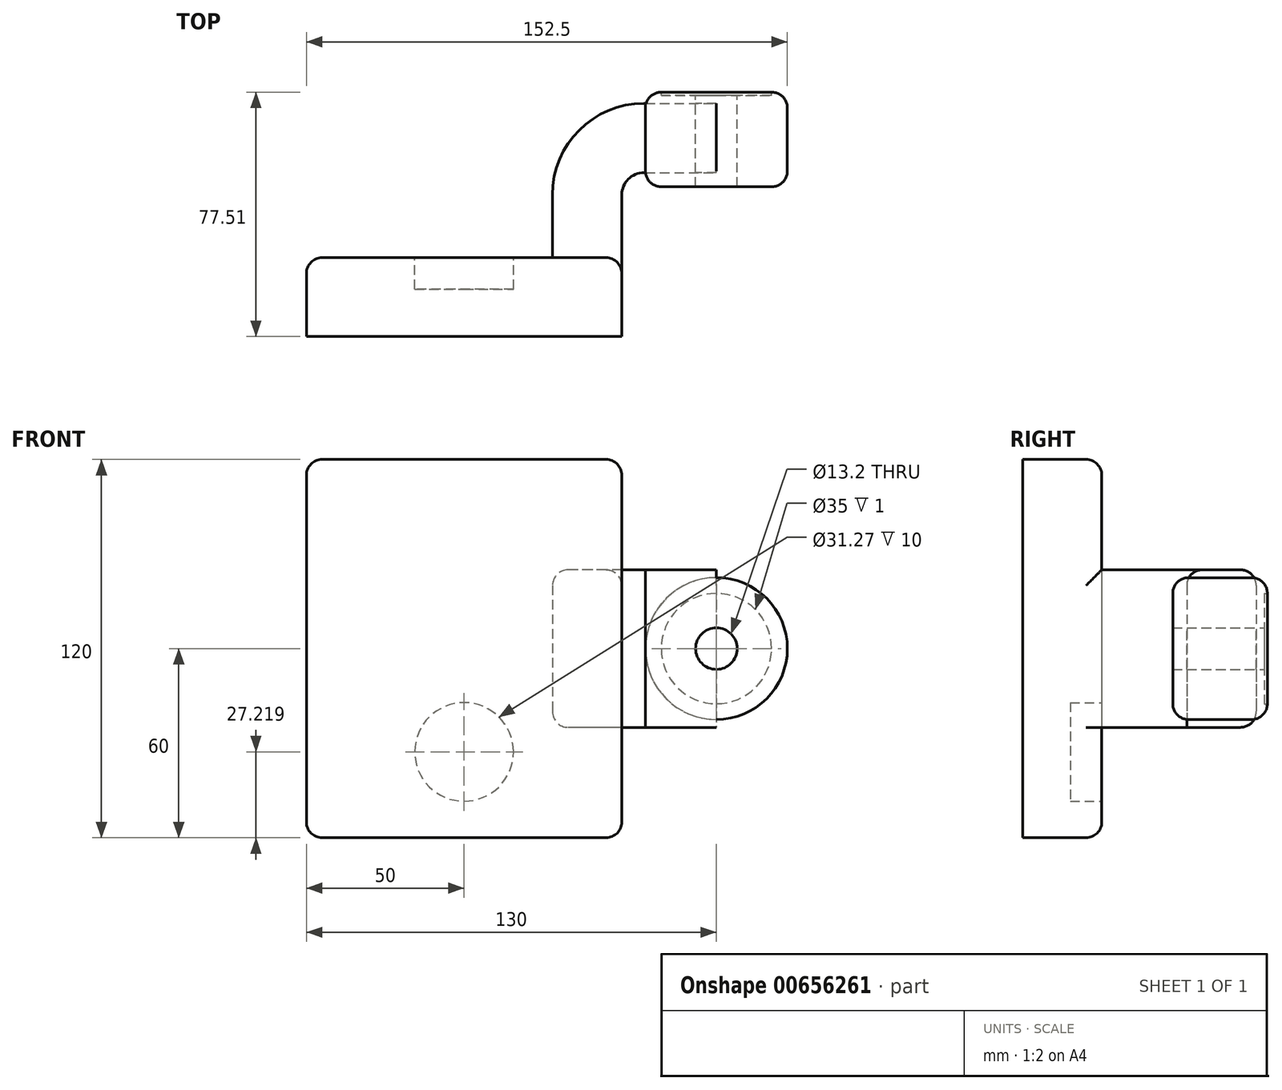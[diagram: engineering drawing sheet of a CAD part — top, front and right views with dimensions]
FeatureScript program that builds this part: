
annotation { "Feature Type Name" : "Feature", "Feature Type Description" : "" }
export const myFeature = defineFeature(function(context is Context, id is Id, definition is map)
    precondition{}
    {
        {
            var Q0;
            Q0=qCreatedBy(makeId("Top.planeOp"),FACE);
            var sketch = newSketch(context, id + "F0", { "sketchPlane" : qUnion([Q0])});
            skLineSegment(sketch, "E0.bottom", {"start": v(50, -12.5) * mm, "end": v(-50, -12.5) * mm});
            skLineSegment(sketch, "E0.top", {"start": v(50, 12.5) * mm, "end": v(-50, 12.5) * mm});
            skLineSegment(sketch, "E0.left", {"start": v(50, -12.5) * mm, "end": v(50, 12.5) * mm});
            skLineSegment(sketch, "E0.right", {"start": v(-50, -12.5) * mm, "end": v(-50, 12.5) * mm});
            skPoint(sketch, "E0.middle", {"position": v(0, 0) * mm});
            skLineSegment(sketch, "E1.bottom", {"start": v(102.5, 35.01) * mm, "end": v(57.5, 35.01) * mm});
            skLineSegment(sketch, "E1.top", {"start": v(102.5, 65.01) * mm, "end": v(57.5, 65.01) * mm});
            skLineSegment(sketch, "E1.left", {"start": v(102.5, 35.01) * mm, "end": v(102.5, 65.01) * mm});
            skLineSegment(sketch, "E1.right", {"start": v(57.5, 35.01) * mm, "end": v(57.5, 65.01) * mm});
            skPoint(sketch, "E1.middle", {"position": v(80, 50.01) * mm});
            skLineSegment(sketch, "E2", {"start": v(50, 12.5) * mm, "end": v(50, 32.46) * mm});
            skArc(sketch, "E3", {"start": v(50, 32.46) * mm, "mid": v(52.05, 37.41) * mm, "end": v(57, 39.46) * mm});
            skLineSegment(sketch, "E4", {"start": v(57, 39.46) * mm, "end": v(80, 39.46) * mm});
            skLineSegment(sketch, "E5.0", {"start": v(57, 61.46) * mm, "end": v(80, 61.46) * mm});
            skArc(sketch, "E5.1", {"start": v(28, 32.46) * mm, "mid": v(36.5, 52.97) * mm, "end": v(57, 61.46) * mm});
            skLineSegment(sketch, "E5.2", {"start": v(28, 12.5) * mm, "end": v(28, 32.46) * mm});
            skFitSpline(sketch, "E6", {"points": [v(-50, 12.5) * mm, v(57, 61.46) * mm], "startDerivative": vector(71.48, 99.9) * mm, "endDerivative": vector(111.8, -6.45) * mm});
            skLineSegment(sketch, "E7", {"start": v(80, 35.01) * mm, "end": v(80, 65.01) * mm});
            skSolve(sketch);
        }
        {
            var Q0;
            Q0=makeQuery(id+"F0.imprint","IMPRINT",FACE,{"disambiguationData":[TD([[makeQuery(id+"F0.imprint","IMPRINT",EDGE,{"derivedFrom":sQuery(id+"F0.wireOp",EDGE,"E5.1")}),1.0]])]});
            extrude(context, id + "F1", {"entities" : qUnion([Q0]), "endBound" : BoundingType.SYMMETRIC, "depth" : 25 * mm, "offsetDistance" : 25 * mm});
        }
        {
            var Q0;
            Q0=makeQuery(id+"F0.imprint","IMPRINT",FACE,{"disambiguationData":[TD([[makeQuery(id+"F0.imprint","IMPRINT",EDGE,{"derivedFrom":sQuery(id+"F0.wireOp",EDGE,"E0.bottom")}),-1.0]])]});
            extrude(context, id + "F2", {"entities" : qUnion([Q0]), "operationType" : NewBodyOperationType.ADD, "endBound" : BoundingType.SYMMETRIC, "depth" : 120 * mm, "offsetDistance" : 25 * mm});
        }
        {
            var Q0;
            {var subQ1=sQuery(id+"F0.wireOp",EDGE,"E2");Q0=makeQuery(id+"F0.imprint","IMPRINT",FACE,{"disambiguationData":[TD([[makeQuery(id+"F0.imprint","IMPRINT",EDGE,{"derivedFrom":subQ1}),1.0]])]});}
            extrude(context, id + "F3", {"entities" : qUnion([Q0]), "operationType" : NewBodyOperationType.ADD, "endBound" : BoundingType.SYMMETRIC, "depth" : 50 * mm, "offsetDistance" : 25 * mm});
        }
        {
            var Q0;
            {var subQ0=sQuery(id+"F0.wireOp",EDGE,"E1.left");Q0=makeQuery(id+"F0.imprint","IMPRINT",FACE,{"disambiguationData":[TD([[makeQuery(id+"F0.imprint","IMPRINT",EDGE,{"derivedFrom":subQ0}),1.0]])]});}
            var Q1;
            Q1=sQuery(id+"F0.wireOp",EDGE,"E7");
            revolve(context, id + "F4", {"operationType" : NewBodyOperationType.ADD, "entities" : qUnion([Q0]), "axis" : qUnion([Q1]), "revolveType" : RevolveType.FULL});
        }
        {
            var Q0;
            {var subQ0=sQuery(id+"F0.wireOp",EDGE,"E4");var subQ1=sQuery(id+"F0.wireOp",EDGE,"E1.right");var subQ2=makeQuery(id+"F0.imprint","INTERSECT",VERTEX,{"derivedFrom":[subQ1,subQ0]});Q0=makeQuery(id+"F0.imprint","IMPRINT",FACE,{"disambiguationData":[TD([[makeQuery(id+"F0.imprint","IMPRINT",EDGE,{"disambiguationData":[TD([[subQ2,-1.0]])],"derivedFrom":subQ1}),-1.0]])]});}
            extrude(context, id + "F5", {"entities" : qUnion([Q0]), "endBound" : BoundingType.SYMMETRIC, "depth" : 50 * mm, "offsetDistance" : 25 * mm});
        }
        {
            var Q0;
            Q0=makeQuery(id+"F2.opExtrude","CAP_EDGE",EDGE,{"disambiguationData":[OSD([sQuery(id+"F0.wireOp",EDGE,"E0.right")])],"isStart":false});
            var Q1;
            Q1=makeQuery(id+"F2.opExtrude","CAP_EDGE",EDGE,{"disambiguationData":[OSD([sQuery(id+"F0.wireOp",EDGE,"E0.left")])],"isStart":false});
            var Q2;
            Q2=makeQuery(id+"F2.opExtrude","CAP_EDGE",EDGE,{"disambiguationData":[OSD([sQuery(id+"F0.wireOp",EDGE,"E0.left")])],"isStart":true});
            var Q3;
            Q3=makeQuery(id+"F2.opExtrude","CAP_EDGE",EDGE,{"disambiguationData":[OSD([sQuery(id+"F0.wireOp",EDGE,"E0.right")])],"isStart":true});
            var Q4;
            Q4=makeQuery(id+"F4.opRevolve","SWEPT_FACE",FACE,{"disambiguationData":[OSD([sQuery(id+"F0.wireOp",EDGE,"E1.top")])]});
            var Q5;
            Q5=makeQuery(id+"F4.opRevolve","SWEPT_FACE",FACE,{"disambiguationData":[OSD([sQuery(id+"F0.wireOp",EDGE,"E1.bottom")])]});
            var Q6;
            Q6=makeQuery(id+"F1.opExtrude","CAP_EDGE",EDGE,{"disambiguationData":[OSD([sQuery(id+"F0.wireOp",EDGE,"E6")])],"isStart":false});
            var Q7;
            Q7=makeQuery(id+"F1.opExtrude","CAP_EDGE",EDGE,{"disambiguationData":[OSD([sQuery(id+"F0.wireOp",EDGE,"E6")])],"isStart":true});
            var Q8;
            Q8=makeQuery(id+"F3.opExtrude","CAP_EDGE",EDGE,{"disambiguationData":[OSD([sQuery(id+"F0.wireOp",EDGE,"E5.1")])],"isStart":false});
            var Q9;
            Q9=makeQuery(id+"F5.opExtrude","CAP_EDGE",EDGE,{"disambiguationData":[OSD([sQuery(id+"F0.wireOp",EDGE,"E5.0")])],"isStart":false});
            var Q10;
            Q10=makeQuery(id+"F5.opExtrude","CAP_EDGE",EDGE,{"disambiguationData":[OSD([sQuery(id+"F0.wireOp",EDGE,"E4")])],"isStart":false});
            var Q11;
            Q11=makeQuery(id+"F3.opExtrude","CAP_EDGE",EDGE,{"disambiguationData":[OSD([sQuery(id+"F0.wireOp",EDGE,"E3")])],"isStart":false});
            var Q12;
            {var subQ0=sQuery(id+"F0.wireOp",EDGE,"E2");var subQ1=sQuery(id+"F0.wireOp",EDGE,"E0.top");var subQ2=sQuery(id+"F0.wireOp",EDGE,"E0.left");Q12=makeQuery(id+"F3.boolean.opBoolean","SPLIT",EDGE,{"disambiguationData":[TD([makeQuery(id+"F2.opExtrude","CAP_FACE",FACE,{"disambiguationData":[OSD([sQuery(id+"F0.wireOp",EDGE,"E0.bottom"),subQ1,subQ2,sQuery(id+"F0.wireOp",EDGE,"E0.right")])],"isStart":false})])],"derivedFrom":makeQuery(id+"F2.opExtrude","SWEPT_EDGE",EDGE,{"disambiguationData":[OSD([subQ1,subQ2,subQ0])]})});}
            var Q13;
            Q13=makeQuery(id+"F2.opExtrude","CAP_EDGE",EDGE,{"disambiguationData":[OSD([sQuery(id+"F0.wireOp",EDGE,"E0.top")])],"isStart":false});
            var Q14;
            {var subQ0=sQuery(id+"F0.wireOp",EDGE,"E0.left");var subQ1=sQuery(id+"F0.wireOp",EDGE,"E2");var subQ2=sQuery(id+"F0.wireOp",EDGE,"E0.top");Q14=makeQuery(id+"F3.boolean.opBoolean","SPLIT",EDGE,{"disambiguationData":[TD([makeQuery(id+"F2.opExtrude","CAP_FACE",FACE,{"disambiguationData":[OSD([sQuery(id+"F0.wireOp",EDGE,"E0.bottom"),subQ2,subQ0,sQuery(id+"F0.wireOp",EDGE,"E0.right")])],"isStart":true})])],"derivedFrom":makeQuery(id+"F2.opExtrude","SWEPT_EDGE",EDGE,{"disambiguationData":[OSD([subQ2,subQ0,subQ1])]})});}
            var Q15;
            Q15=makeQuery(id+"F2.opExtrude","CAP_EDGE",EDGE,{"disambiguationData":[OSD([sQuery(id+"F0.wireOp",EDGE,"E0.top")])],"isStart":true});
            fillet(context, id + "F6", {"entities" : qUnion([Q0, Q1, Q2, Q3, Q4, Q5, Q6, Q7, Q8, Q9, Q10, Q11, Q12, Q13, Q14, Q15]), "radius" : 5 * mm, "tangentPropagation" : true, "allowEdgeOverflow" : false});
        }
        {
            var Q0;
            {var subQ0=sQuery(id+"F0.wireOp",EDGE,"E0.top");var subQ1=sQuery(id+"F0.wireOp",EDGE,"E0.right");var subQ2=sQuery(id+"F0.wireOp",EDGE,"E6");Q0=makeQuery(id+"F2.boolean.opBoolean","SPLIT",EDGE,{"disambiguationData":[TD([makeQuery(id+"F1.opExtrude","CAP_FACE",FACE,{"disambiguationData":[OSD([subQ0,sQuery(id+"F0.wireOp",EDGE,"E5.1"),sQuery(id+"F0.wireOp",EDGE,"E5.2"),subQ2])],"isStart":false})])],"derivedFrom":makeQuery(id+"F2.opExtrude","SWEPT_EDGE",EDGE,{"disambiguationData":[OSD([subQ0,subQ1,subQ2])]})});}
            var Q1;
            {var subQ0=sQuery(id+"F0.wireOp",EDGE,"E0.top");var subQ1=sQuery(id+"F0.wireOp",EDGE,"E0.right");var subQ2=sQuery(id+"F0.wireOp",EDGE,"E6");Q1=makeQuery(id+"F2.boolean.opBoolean","SPLIT",EDGE,{"disambiguationData":[TD([makeQuery(id+"F1.opExtrude","CAP_FACE",FACE,{"disambiguationData":[OSD([subQ0,sQuery(id+"F0.wireOp",EDGE,"E5.1"),sQuery(id+"F0.wireOp",EDGE,"E5.2"),subQ2])],"isStart":true})])],"derivedFrom":makeQuery(id+"F2.opExtrude","SWEPT_EDGE",EDGE,{"disambiguationData":[OSD([subQ0,subQ1,subQ2])]})});}
            fillet(context, id + "F7", {"entities" : qUnion([Q0, Q1]), "radius" : 5 * mm, "tangentPropagation" : true, "allowEdgeOverflow" : false});
        }
        {
            var Q0;
            Q0=makeQuery(id+"F4.opRevolve","SWEPT_FACE",FACE,{"disambiguationData":[OSD([sQuery(id+"F0.wireOp",EDGE,"E1.top")])]});
            var sketch = newSketch(context, id + "F8", { "sketchPlane" : qUnion([Q0])});
            skPoint(sketch, "E8", {"position": v(-80, 0) * mm});
            skSolve(sketch);
        }
        {
            var Q0;
            Q0=sQuery(id+"F8.wireOp",VERTEX,"E8");
            var Q1;
            Q1=makeQuery(id+"F4.opRevolve","SWEPT_BODY",BODY,{"disambiguationData":[OSD([sQuery(id+"F0.wireOp",EDGE,"E1.bottom"),sQuery(id+"F0.wireOp",EDGE,"E1.top"),sQuery(id+"F0.wireOp",EDGE,"E1.left"),sQuery(id+"F0.wireOp",EDGE,"E7")])]});
            var Q2;
            Q2=makeQuery(id+"F5.opExtrude","SWEPT_BODY",BODY,{"disambiguationData":[OSD([sQuery(id+"F0.wireOp",EDGE,"E1.right"),sQuery(id+"F0.wireOp",EDGE,"E4"),sQuery(id+"F0.wireOp",EDGE,"E5.0"),sQuery(id+"F0.wireOp",EDGE,"E7")])]});
            hole(context, id + "F9", {"style" : HoleStyle.SIMPLE, "endStyle" : HoleEndStyle.THROUGH, "standardTappedOrClearance" : lookupTablePath({ "standard" : "ISO", "fit" : "Normal", "size" : "M12", "type" : "Clearance" }), "standardBlindInLast" : lookupTablePath({ "fit" : "Standard", "standard" : "ISO", "size" : "M12", "type" : "Clearance" }), "holeDiameter" : 13.2 * mm, "majorDiameter" : 10 * mm, "isTappedThrough" : true, "tappedDepth" : 12 * mm, "tapClearance" : 3, "startFromSketch" : true, "locations" : qUnion([Q0]), "scope" : qUnion([Q1, Q2])});
        }
        {
            var Q0;
            Q0=makeQuery(id+"F5.opExtrude","CAP_EDGE",EDGE,{"disambiguationData":[OSD([sQuery(id+"F0.wireOp",EDGE,"E5.0")])],"isStart":true});
            var Q1;
            Q1=makeQuery(id+"F3.opExtrude","CAP_EDGE",EDGE,{"disambiguationData":[OSD([sQuery(id+"F0.wireOp",EDGE,"E5.1")])],"isStart":true});
            fillet(context, id + "F10", {"entities" : qUnion([Q0, Q1]), "radius" : 5 * mm, "tangentPropagation" : true, "allowEdgeOverflow" : false});
        }
        {
            var Q0;
            Q0=makeQuery(id+"F4.opRevolve","SWEPT_FACE",FACE,{"disambiguationData":[OSD([sQuery(id+"F0.wireOp",EDGE,"E1.top")])]});
            extrude(context, id + "F11", {"entities" : qUnion([Q0]), "operationType" : NewBodyOperationType.REMOVE, "oppositeDirection" : true, "depth" : 1 * mm, "offsetDistance" : 25 * mm});
        }
        {
            var Q0;
            {var subQ2=sQuery(id+"F0.wireOp",EDGE,"E0.top");var subQ3=sQuery(id+"F0.wireOp",EDGE,"E6");var subQ5=sQuery(id+"F0.wireOp",EDGE,"E5.2");var subQ6=sQuery(id+"F0.wireOp",EDGE,"E5.1");Q0=makeQuery(id+"F3.boolean.opBoolean","SPLIT",FACE,{"disambiguationData":[TD([makeQuery(id+"F1.opExtrude","CAP_FACE",FACE,{"disambiguationData":[OSD([subQ2,subQ6,subQ5,subQ3])],"isStart":true})])],"derivedFrom":makeQuery(id+"F2.opExtrude","SWEPT_FACE",FACE,{"disambiguationData":[OSD([subQ2])]})});}
            var sketch = newSketch(context, id + "F12", { "sketchPlane" : qUnion([Q0])});
            skCircle(sketch, "E9", {"center": v(0, -32.78) * mm, "radius": 15.64 * mm});
            skSolve(sketch);
        }
        {
            var Q0;
            Q0=makeQuery(id+"F12.imprint","IMPRINT",FACE,{"disambiguationData":[TD([[makeQuery(id+"F12.imprint","IMPRINT",EDGE,{"derivedFrom":sQuery(id+"F12.wireOp",EDGE,"E9")}),1.0]])]});
            extrude(context, id + "F13", {"entities" : qUnion([Q0]), "operationType" : NewBodyOperationType.REMOVE, "oppositeDirection" : true, "depth" : 10 * mm, "offsetDistance" : 25 * mm});
        }
    });
